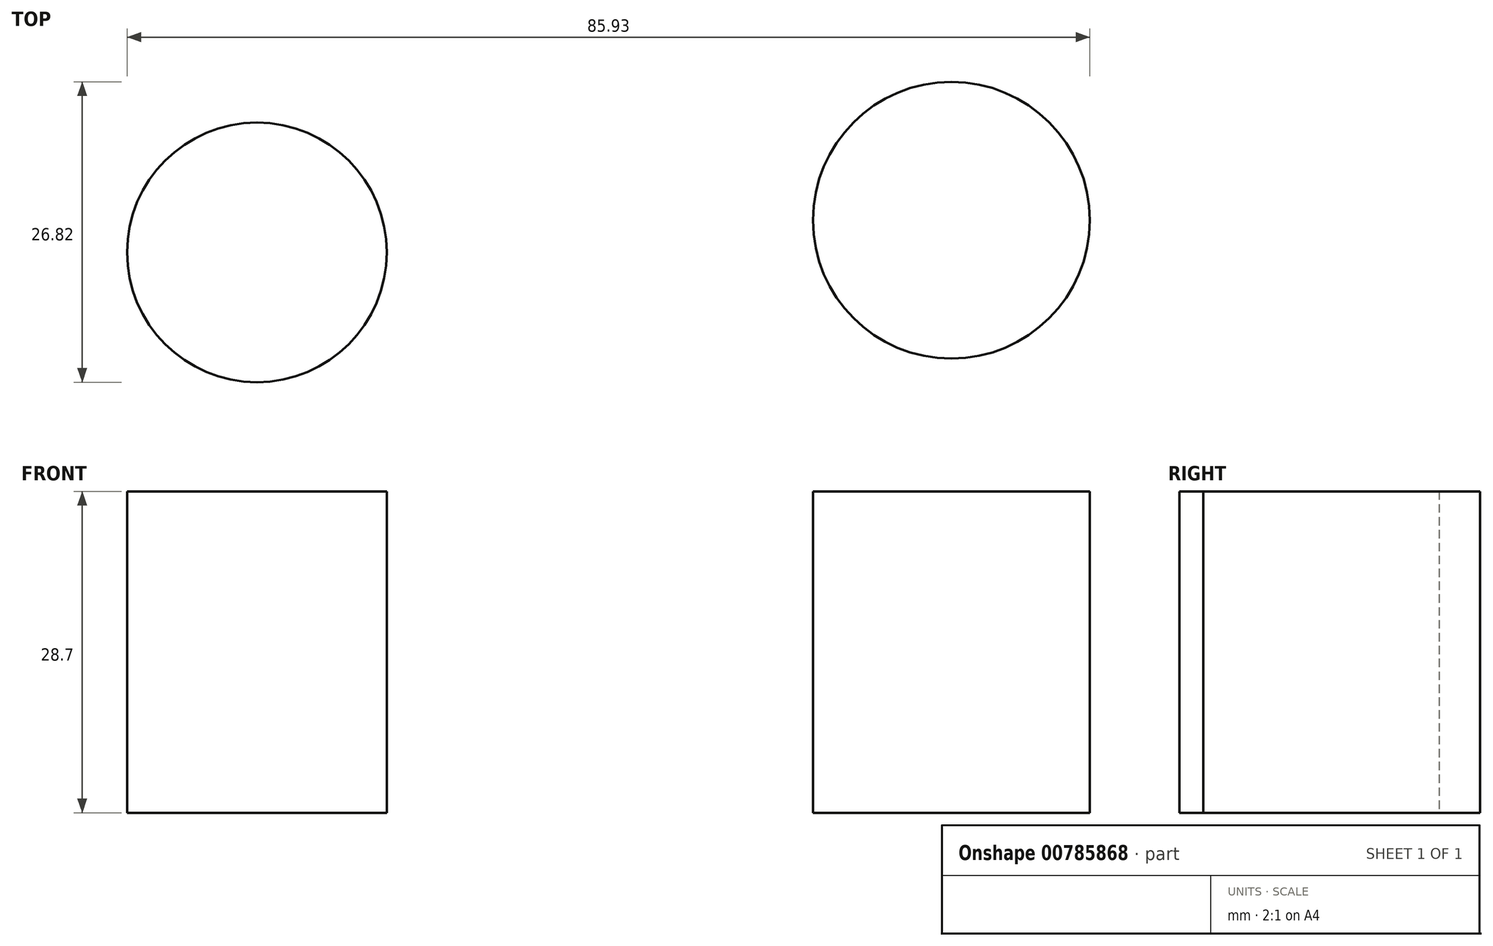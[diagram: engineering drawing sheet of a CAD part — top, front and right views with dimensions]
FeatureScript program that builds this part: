
annotation { "Feature Type Name" : "Feature", "Feature Type Description" : "" }
export const myFeature = defineFeature(function(context is Context, id is Id, definition is map)
    precondition{}
    {
        {
            var Q0;
            Q0=qCreatedBy(makeId("Top.planeOp"),FACE);
            var sketch = newSketch(context, id + "F0", { "sketchPlane" : qUnion([Q0])});
            skCircle(sketch, "E0", {"center": v(-55.4, 14.84) * mm, "radius": 11.59 * mm});
            skCircle(sketch, "E1", {"center": v(6.58, 17.71) * mm, "radius": 12.35 * mm});
            skSolve(sketch);
        }
        {
            var Q0;
            Q0=makeQuery(id+"F0.imprint","IMPRINT",FACE,{"disambiguationData":[TD([[makeQuery(id+"F0.imprint","IMPRINT",EDGE,{"derivedFrom":sQuery(id+"F0.wireOp",EDGE,"E0")}),1.0]])]});
            var Q1;
            Q1=makeQuery(id+"F0.imprint","IMPRINT",FACE,{"disambiguationData":[TD([[makeQuery(id+"F0.imprint","IMPRINT",EDGE,{"derivedFrom":sQuery(id+"F0.wireOp",EDGE,"E1")}),1.0]])]});
            extrude(context, id + "F1", {"entities" : qUnion([Q0, Q1]), "depth" : 28.7 * mm, "offsetDistance" : 25.4 * mm});
        }
    });
